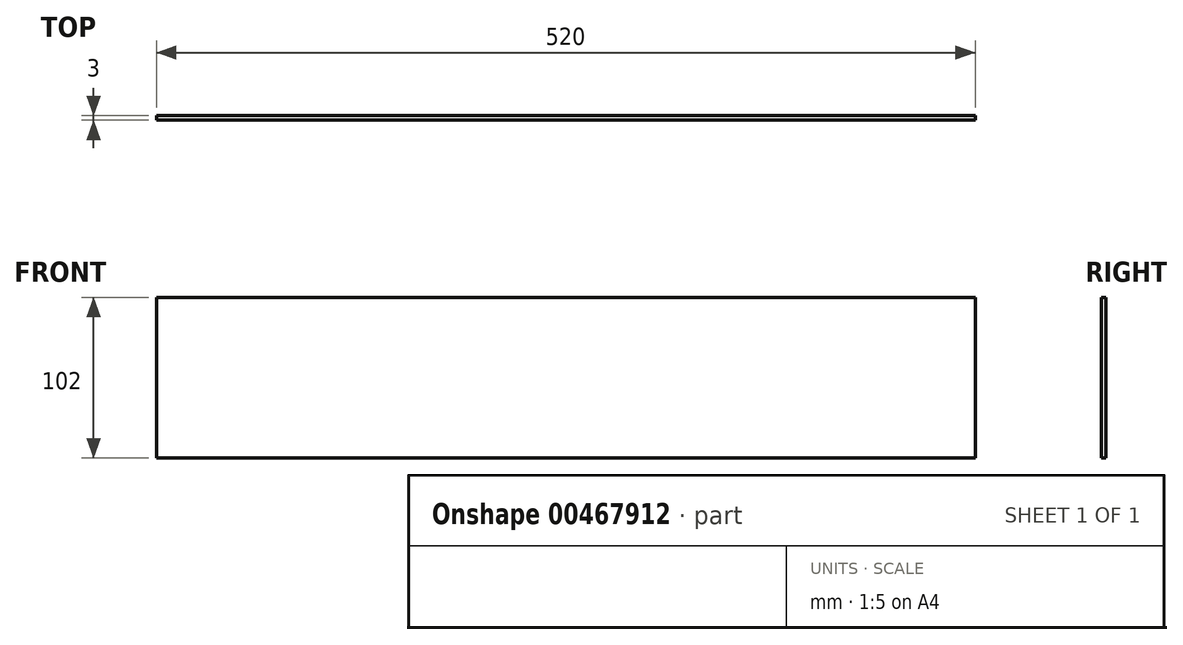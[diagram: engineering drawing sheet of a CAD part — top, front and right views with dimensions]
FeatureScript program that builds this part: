
annotation { "Feature Type Name" : "Feature", "Feature Type Description" : "" }
export const myFeature = defineFeature(function(context is Context, id is Id, definition is map)
    precondition{}
    {
        {
            var Q0;
            Q0=qCreatedBy(makeId("Front.planeOp"),FACE);
            var sketch = newSketch(context, id + "F0", { "sketchPlane" : qUnion([Q0])});
            skLineSegment(sketch, "E0.bottom", {"start": v(-49.8, -41.22) * mm, "end": v(80.2, -41.22) * mm});
            skLineSegment(sketch, "E0.top", {"start": v(-49.8, 60.78) * mm, "end": v(80.2, 60.78) * mm});
            skLineSegment(sketch, "E0.left", {"start": v(-49.8, -41.22) * mm, "end": v(-49.8, 60.78) * mm});
            skLineSegment(sketch, "E0.right", {"start": v(80.2, -41.22) * mm, "end": v(80.2, 60.78) * mm});
            skLineSegment(sketch, "E1.bottom", {"start": v(80.2, -41.22) * mm, "end": v(210.2, -41.22) * mm});
            skLineSegment(sketch, "E1.top", {"start": v(80.2, 60.78) * mm, "end": v(210.2, 60.78) * mm});
            skLineSegment(sketch, "E1.right", {"start": v(210.2, -41.22) * mm, "end": v(210.2, 60.78) * mm});
            skLineSegment(sketch, "E2.bottom", {"start": v(-49.8, -41.22) * mm, "end": v(-179.8, -41.22) * mm});
            skLineSegment(sketch, "E2.top", {"start": v(-49.8, 60.78) * mm, "end": v(-179.8, 60.78) * mm});
            skLineSegment(sketch, "E2.right", {"start": v(-179.8, -41.22) * mm, "end": v(-179.8, 60.78) * mm});
            skLineSegment(sketch, "E3.bottom", {"start": v(210.2, -41.22) * mm, "end": v(340.2, -41.22) * mm});
            skLineSegment(sketch, "E3.top", {"start": v(210.2, 60.78) * mm, "end": v(340.2, 60.78) * mm});
            skLineSegment(sketch, "E3.right", {"start": v(340.2, -41.22) * mm, "end": v(340.2, 60.78) * mm});
            skSolve(sketch);
        }
        {
            var Q0;
            Q0=makeQuery(id+"F0.imprint","IMPRINT",FACE,{"disambiguationData":[TD([[makeQuery(id+"F0.imprint","IMPRINT",EDGE,{"derivedFrom":sQuery(id+"F0.wireOp",EDGE,"E2.bottom")}),-1.0]])]});
            var Q1;
            Q1=makeQuery(id+"F0.imprint","IMPRINT",FACE,{"disambiguationData":[TD([[makeQuery(id+"F0.imprint","IMPRINT",EDGE,{"derivedFrom":sQuery(id+"F0.wireOp",EDGE,"E0.bottom")}),1.0]])]});
            var Q2;
            Q2=makeQuery(id+"F0.imprint","IMPRINT",FACE,{"disambiguationData":[TD([[makeQuery(id+"F0.imprint","IMPRINT",EDGE,{"derivedFrom":sQuery(id+"F0.wireOp",EDGE,"E1.bottom")}),1.0]])]});
            var Q3;
            Q3=makeQuery(id+"F0.imprint","IMPRINT",FACE,{"disambiguationData":[TD([[makeQuery(id+"F0.imprint","IMPRINT",EDGE,{"derivedFrom":sQuery(id+"F0.wireOp",EDGE,"E3.bottom")}),1.0]])]});
            extrude(context, id + "F1", {"entities" : qUnion([Q0, Q1, Q2, Q3]), "depth" : 3 * mm, "offsetDistance" : 25 * mm});
        }
    });
